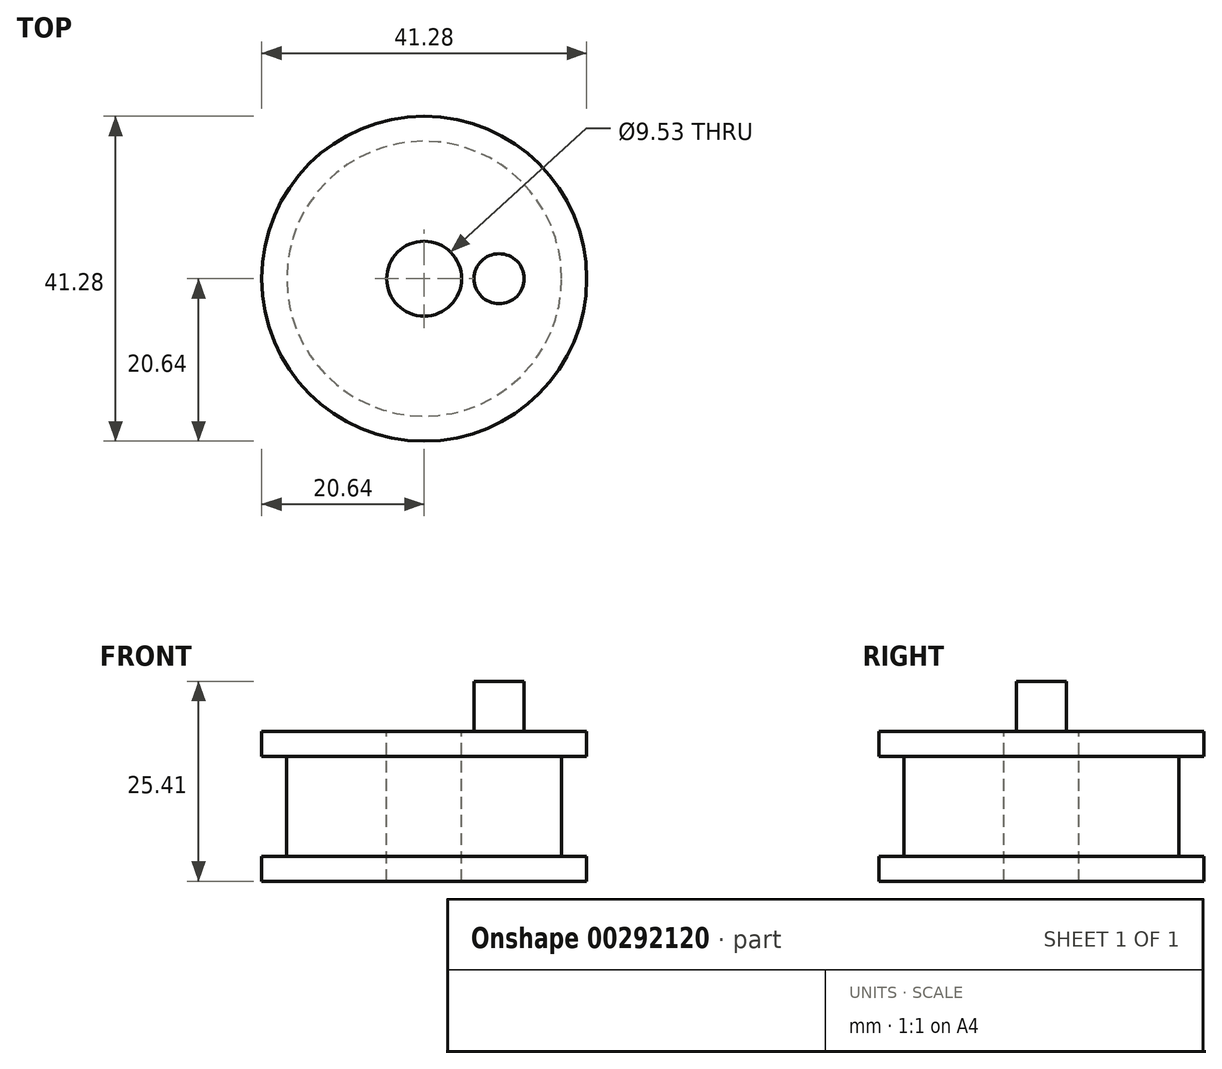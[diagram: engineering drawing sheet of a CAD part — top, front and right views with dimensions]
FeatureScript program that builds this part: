
annotation { "Feature Type Name" : "Feature", "Feature Type Description" : "" }
export const myFeature = defineFeature(function(context is Context, id is Id, definition is map)
    precondition{}
    {
        {
            var Q0;
            Q0=qCreatedBy(makeId("Front.planeOp"),FACE);
            var sketch = newSketch(context, id + "F0", { "sketchPlane" : qUnion([Q0])});
            skLineSegment(sketch, "E0.bottom", {"start": v(4.76, 6.35) * mm, "end": v(17.46, 6.35) * mm});
            skLineSegment(sketch, "E0.top", {"start": v(4.76, -6.35) * mm, "end": v(17.46, -6.35) * mm});
            skLineSegment(sketch, "E0.left", {"start": v(4.76, 6.35) * mm, "end": v(4.76, -6.35) * mm});
            skLineSegment(sketch, "E0.right", {"start": v(17.46, 6.35) * mm, "end": v(17.46, -6.35) * mm});
            skLineSegment(sketch, "E1.bottom", {"start": v(4.76, 6.35) * mm, "end": v(20.64, 6.35) * mm});
            skLineSegment(sketch, "E1.top", {"start": v(4.76, 9.53) * mm, "end": v(20.64, 9.53) * mm});
            skLineSegment(sketch, "E1.left", {"start": v(4.76, 6.35) * mm, "end": v(4.76, 9.53) * mm});
            skLineSegment(sketch, "E1.right", {"start": v(20.64, 6.35) * mm, "end": v(20.64, 9.53) * mm});
            skLineSegment(sketch, "E2.bottom", {"start": v(4.76, -6.35) * mm, "end": v(20.64, -6.35) * mm});
            skLineSegment(sketch, "E2.top", {"start": v(4.76, -9.53) * mm, "end": v(20.64, -9.53) * mm});
            skLineSegment(sketch, "E2.left", {"start": v(4.76, -6.35) * mm, "end": v(4.76, -9.53) * mm});
            skLineSegment(sketch, "E2.right", {"start": v(20.64, -6.35) * mm, "end": v(20.64, -9.53) * mm});
            skLineSegment(sketch, "E3.bottom", {"start": v(4.76, 9.53) * mm, "end": v(0, 9.53) * mm});
            skLineSegment(sketch, "E3.top", {"start": v(4.76, -9.53) * mm, "end": v(0, -9.53) * mm});
            skLineSegment(sketch, "E3.left", {"start": v(4.76, 9.53) * mm, "end": v(4.76, -9.53) * mm});
            skLineSegment(sketch, "E3.right", {"start": v(0, 9.53) * mm, "end": v(0, -9.53) * mm});
            skSolve(sketch);
        }
        {
            var Q0;
            {var subQ1=sQuery(id+"F0.wireOp",EDGE,"E1.top");Q0=makeQuery(id+"F0.imprint","IMPRINT",FACE,{"disambiguationData":[TD([[makeQuery(id+"F0.imprint","IMPRINT",EDGE,{"derivedFrom":subQ1}),-1.0]])]});}
            var Q1;
            {var subQ0=sQuery(id+"F0.wireOp",EDGE,"E0.right");Q1=makeQuery(id+"F0.imprint","IMPRINT",FACE,{"disambiguationData":[TD([[makeQuery(id+"F0.imprint","IMPRINT",EDGE,{"derivedFrom":subQ0}),-1.0]])]});}
            var Q2;
            {var subQ1=sQuery(id+"F0.wireOp",EDGE,"E2.top");Q2=makeQuery(id+"F0.imprint","IMPRINT",FACE,{"disambiguationData":[TD([[makeQuery(id+"F0.imprint","IMPRINT",EDGE,{"derivedFrom":subQ1}),1.0]])]});}
            var Q3;
            Q3=sQuery(id+"F0.wireOp",EDGE,"E3.right");
            revolve(context, id + "F1", {"entities" : qUnion([Q0, Q1, Q2]), "axis" : qUnion([Q3]), "revolveType" : RevolveType.FULL});
        }
        {
            var Q0;
            Q0=makeQuery(id+"F1.opRevolve","SWEPT_FACE",FACE,{"disambiguationData":[OSD([sQuery(id+"F0.wireOp",EDGE,"E1.top")])]});
            var sketch = newSketch(context, id + "F2", { "sketchPlane" : qUnion([Q0])});
            skCircle(sketch, "E4", {"center": v(9.53, 0) * mm, "radius": 3.18 * mm});
            skSolve(sketch);
        }
        {
            var Q0;
            Q0 = qSketchRegion(id + "F2", true);
            extrude(context, id + "F3", {"entities" : qUnion([Q0]), "operationType" : NewBodyOperationType.ADD, "depth" : 6.35 * mm});
        }
    });
